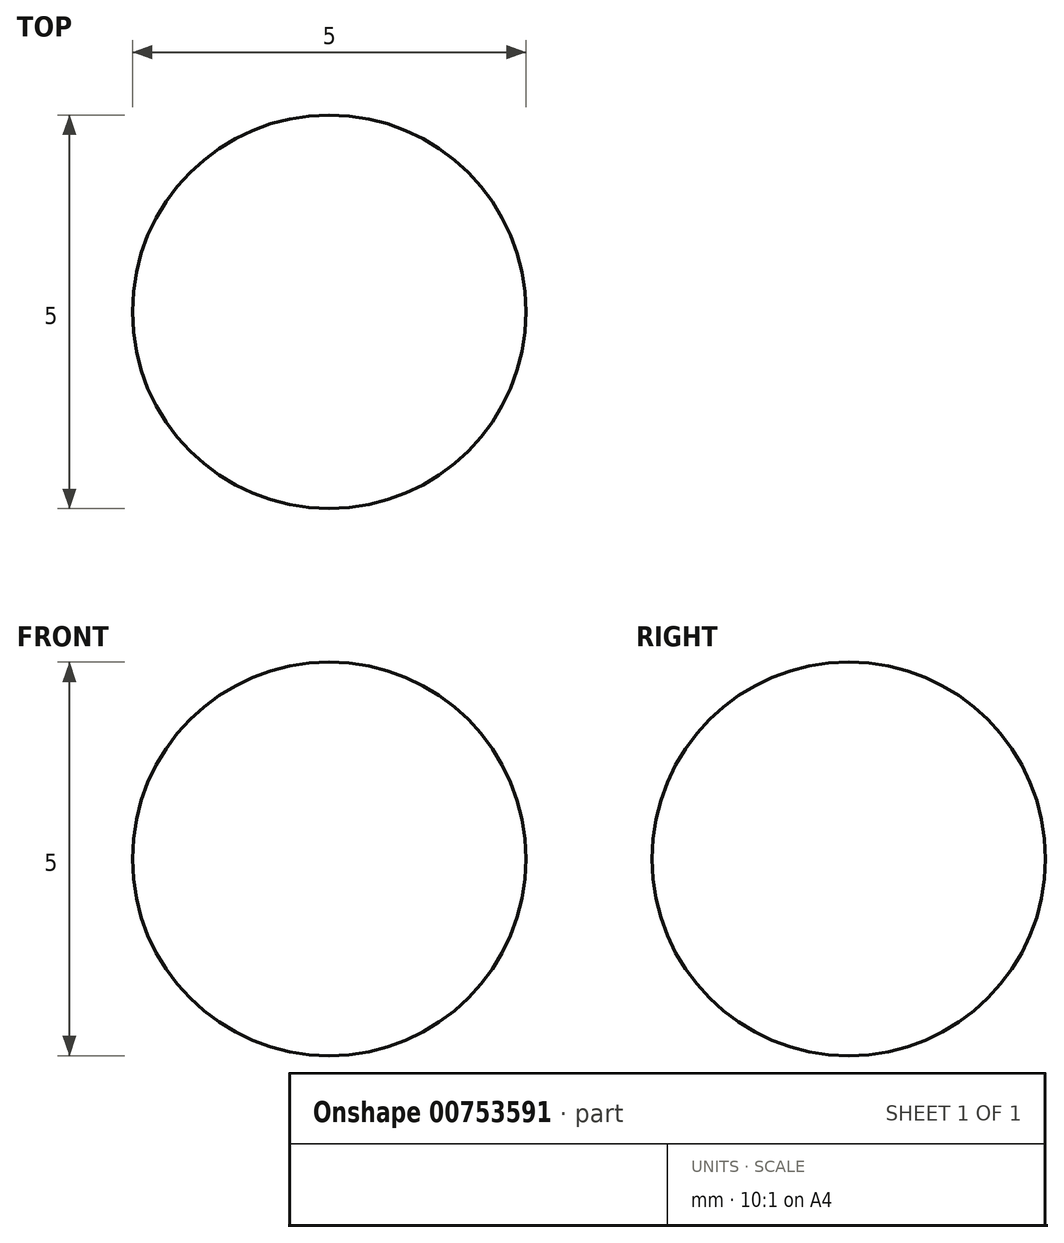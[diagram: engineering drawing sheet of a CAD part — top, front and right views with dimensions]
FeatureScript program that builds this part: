
annotation { "Feature Type Name" : "Feature", "Feature Type Description" : "" }
export const myFeature = defineFeature(function(context is Context, id is Id, definition is map)
    precondition{}
    {
        {
            var Q0;
            Q0=qCreatedBy(makeId("Front.planeOp"),FACE);
            var sketch = newSketch(context, id + "F0", { "sketchPlane" : qUnion([Q0])});
            skArc(sketch, "E0", {"start": v(0, -2.5) * mm, "mid": v(2.5, 0) * mm, "end": v(0, 2.5) * mm});
            skLineSegment(sketch, "E1", {"start": v(0, 2.5) * mm, "end": v(0, -2.5) * mm});
            skSolve(sketch);
        }
        {
            var Q0;
            Q0 = qSketchRegion(id + "F0", true);
            var Q1;
            Q1=sQuery(id+"F0.wireOp",EDGE,"E1");
            revolve(context, id + "F1", {"surfaceOperationType" : NewSurfaceOperationType.NEW, "entities" : qUnion([Q0]), "axis" : qUnion([Q1]), "revolveType" : RevolveType.FULL});
        }
    });
